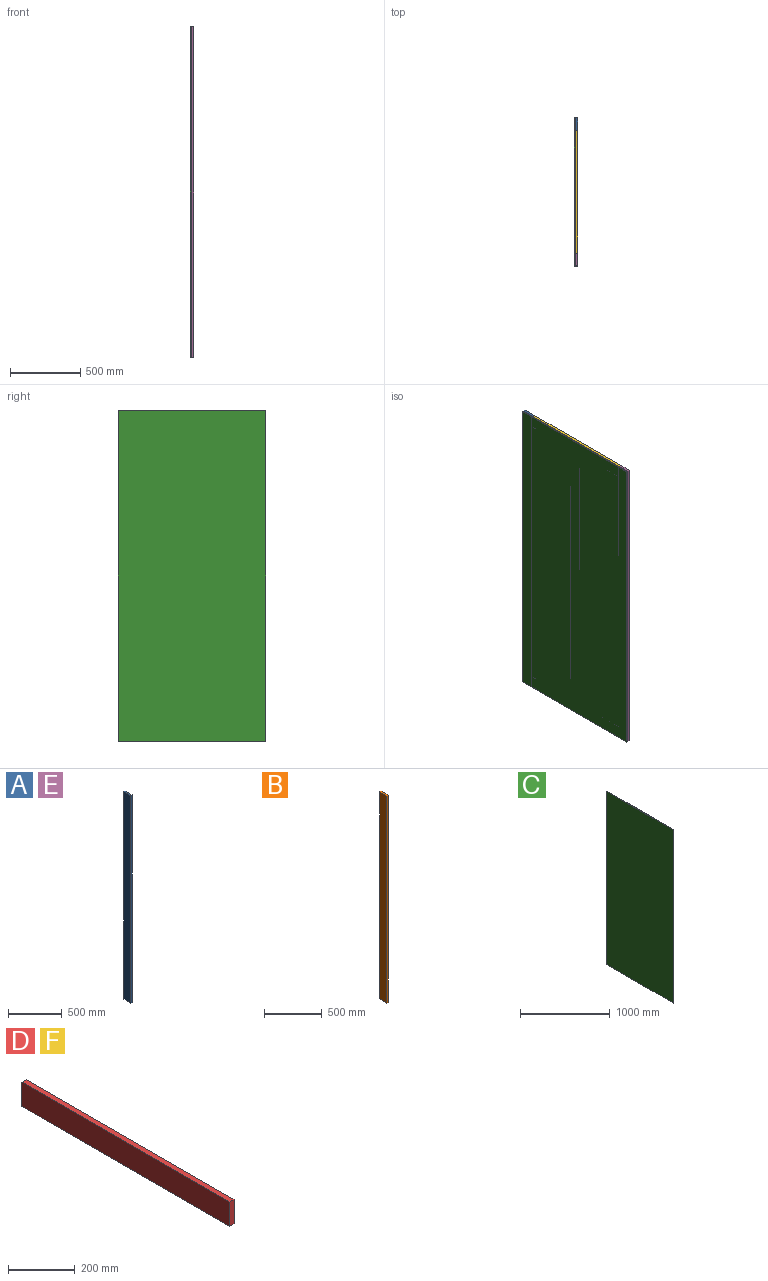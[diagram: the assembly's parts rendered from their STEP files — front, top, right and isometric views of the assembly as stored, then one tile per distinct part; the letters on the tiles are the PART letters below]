
ASSEMBLY  parts=6 mates=5
PART A: 6 faces, bbox 19.1x88.9x2362.2 mm
  f0: plane 2362.2x88.9mm, normal (-1,0,0), area 209999.6mm2, adj f1,f3,f4,f5
  f1: plane 2362.2x19.05mm, normal (0,-1,0), area 44999.9mm2, adj f0,f2,f4,f5
  f2: plane 2362.2x88.9mm, normal (1,0,0), area 209999.6mm2, adj f1,f3,f4,f5
  f3: plane 2362.2x19.05mm, normal (0,1,0), area 44999.9mm2, adj f0,f2,f4,f5
  f4: plane 88.9x19.05mm, normal (0,0,-1), area 1693.5mm2, adj f0,f1,f2,f3
  f5: plane 88.9x19.05mm, normal (0,0,1), area 1693.5mm2, adj f0,f1,f2,f3
PART B: 6 faces, bbox 19.1x88.9x2184.4 mm
  f0: plane 2184.4x88.9mm, normal (-1,0,0), area 194193.2mm2, adj f1,f3,f4,f5
  f1: plane 2184.4x19.05mm, normal (0,-1,0), area 41612.8mm2, adj f0,f2,f4,f5
  f2: plane 2184.4x88.9mm, normal (1,0,0), area 194193.2mm2, adj f1,f3,f4,f5
  f3: plane 2184.4x19.05mm, normal (0,1,0), area 41612.8mm2, adj f0,f2,f4,f5
  f4: plane 88.9x19.05mm, normal (0,0,-1), area 1693.5mm2, adj f0,f1,f2,f3
  f5: plane 88.9x19.05mm, normal (0,0,1), area 1693.5mm2, adj f0,f1,f2,f3
PART C: 6 faces, bbox 6.4x1054.1x2362.2 mm
  f0: plane 1054.1x6.35mm, normal (0,0,1), area 6693.5mm2, adj f1,f3,f4,f5
  f1: plane 2362.2x6.35mm, normal (0,-1,0), area 15000mm2, adj f0,f2,f4,f5
  f2: plane 1054.1x6.35mm, normal (0,0,-1), area 6693.5mm2, adj f1,f3,f4,f5
  f3: plane 2362.2x6.35mm, normal (0,1,0), area 15000mm2, adj f0,f2,f4,f5
  f4: plane 2362.2x1054.1mm, normal (1,0,0), area 2489995mm2, adj f0,f1,f2,f3
  f5: plane 2362.2x1054.1mm, normal (-1,0,0), area 2489995mm2, adj f0,f1,f2,f3
PART D: 6 faces, bbox 19.1x876.3x88.9 mm
  f0: plane 876.3x19.05mm, normal (0,0,1), area 16693.5mm2, adj f1,f3,f4,f5
  f1: plane 876.3x88.9mm, normal (-1,0,0), area 77903.1mm2, adj f0,f2,f4,f5
  f2: plane 876.3x19.05mm, normal (0,0,-1), area 16693.5mm2, adj f1,f3,f4,f5
  f3: plane 876.3x88.9mm, normal (1,0,0), area 77903.1mm2, adj f0,f2,f4,f5
  f4: plane 88.9x19.05mm, normal (0,1,0), area 1693.5mm2, adj f0,f1,f2,f3
  f5: plane 88.9x19.05mm, normal (0,-1,0), area 1693.5mm2, adj f0,f1,f2,f3
PART E: same geometry as A
PART F: same geometry as D
PLACE A t=(-415.73,832.19,2115.21)mm
PLACE B t=(-415.73,363.96,2026.31)mm
PLACE C t=(-422.08,-105.01,-133.87)mm
PLACE D t=(-415.73,-57.27,-228.65)mm
PLACE E t=(-415.73,-133.01,2115.21)mm
PLACE F t=(-415.73,-57.27,2044.65)mm
MATE fastened F.f1 <-> C.f4  axis (-1,0,0) through (-415.73,380.88,2115.21)mm
MATE fastened B.f0 <-> C.f4  axis (-1,0,0) through (-415.73,380.88,934.11)mm
MATE fastened A.f0 <-> C.f4  axis (-1,0,0) through (-415.73,907.93,934.11)mm
MATE fastened E.f0 <-> C.f4  axis (-1,0,0) through (-415.73,-146.17,934.11)mm
MATE fastened D.f1 <-> C.f4  axis (-1,0,0) through (-415.73,380.88,-246.99)mm
